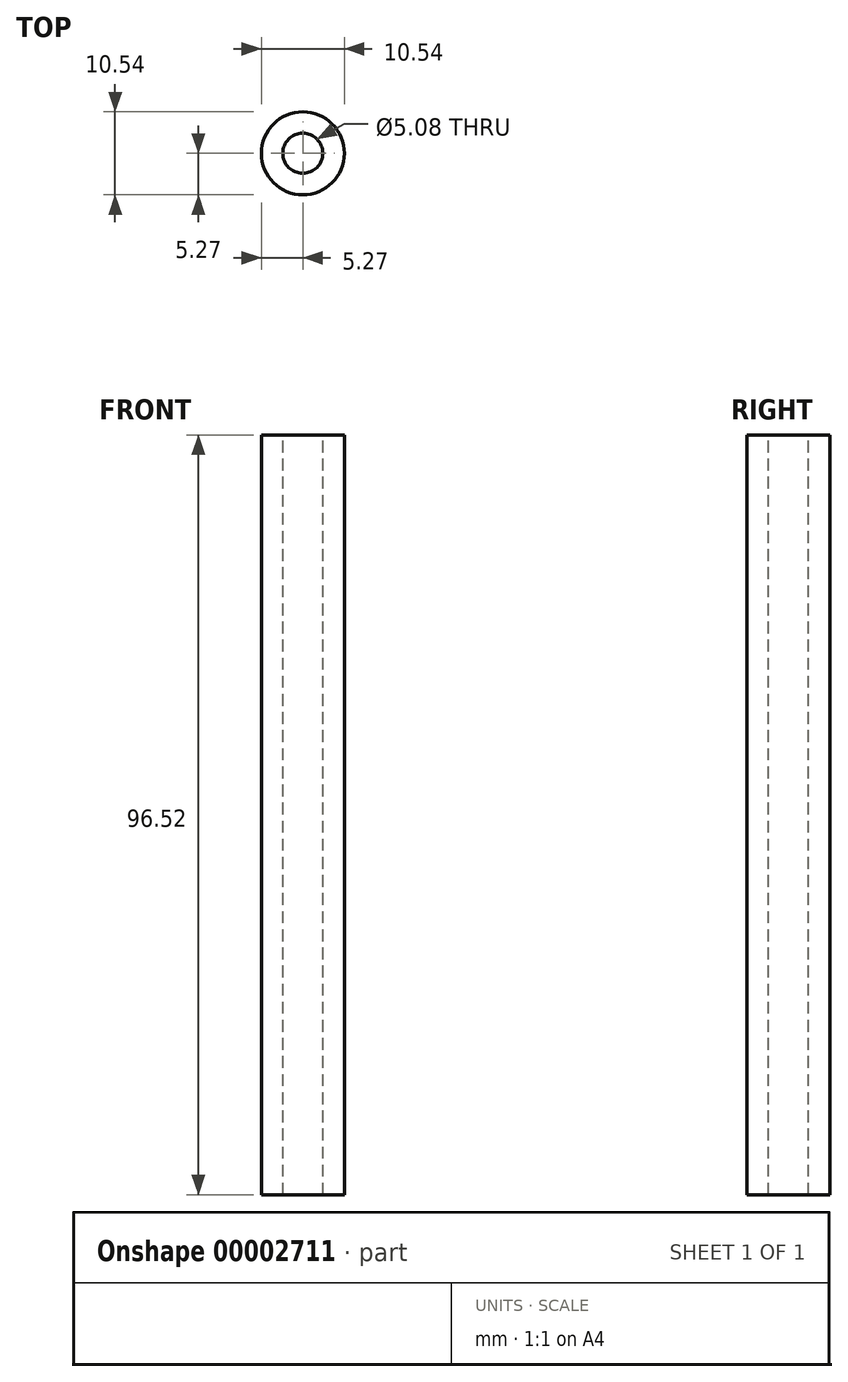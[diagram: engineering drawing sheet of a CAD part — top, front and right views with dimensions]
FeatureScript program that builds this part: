
annotation { "Feature Type Name" : "Feature", "Feature Type Description" : "" }
export const myFeature = defineFeature(function(context is Context, id is Id, definition is map)
    precondition{}
    {
        {
            var Q0;
            Q0=qCreatedBy(makeId("Top.planeOp"),FACE);
            var sketch = newSketch(context, id + "F0", { "sketchPlane" : qUnion([Q0])});
            skCircle(sketch, "E0", {"center": v(0, 0) * mm, "radius": 5.27 * mm});
            skSolve(sketch);
        }
        {
            var Q0;
            Q0 = qSketchRegion(id + "F0", true);
            extrude(context, id + "F1", {"entities" : qUnion([Q0]), "depth" : 96.52 * mm});
        }
        {
            var Q0;
            Q0=makeQuery(id+"F1.opExtrude","CAP_FACE",FACE,{"disambiguationData":[OSD([sQuery(id+"F0.wireOp",EDGE,"E0")])],"isStart":false});
            var sketch = newSketch(context, id + "F2", { "sketchPlane" : qUnion([Q0])});
            skCircle(sketch, "E1", {"center": v(0, 0) * mm, "radius": 2.54 * mm});
            skSolve(sketch);
        }
        {
            var Q0;
            Q0=makeQuery(id+"F2.imprint","IMPRINT",FACE,{"disambiguationData":[TD([[makeQuery(id+"F2.imprint","IMPRINT",EDGE,{"derivedFrom":sQuery(id+"F2.wireOp",EDGE,"E1")}),1.0]])]});
            extrude(context, id + "F3", {"entities" : qUnion([Q0]), "operationType" : NewBodyOperationType.REMOVE, "endBound" : BoundingType.THROUGH_ALL, "oppositeDirection" : true, "depth" : 25.4 * mm});
        }
    });
